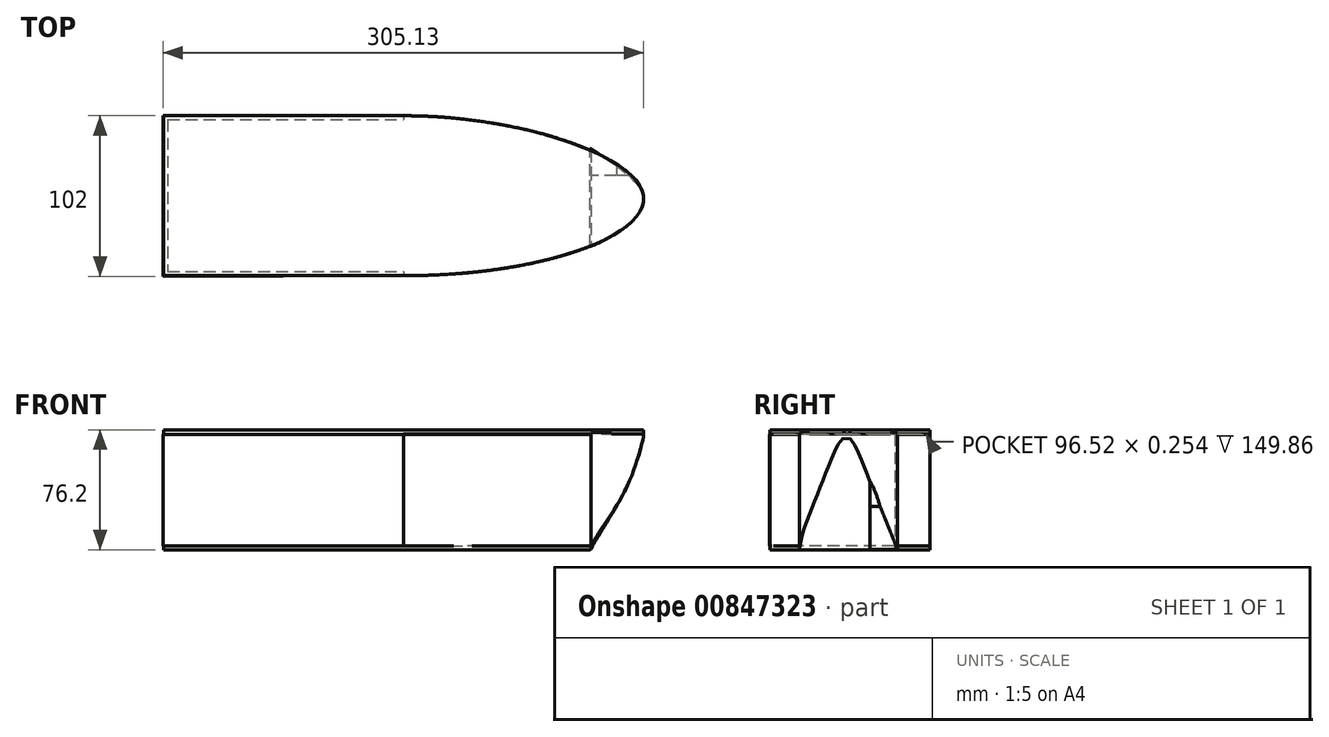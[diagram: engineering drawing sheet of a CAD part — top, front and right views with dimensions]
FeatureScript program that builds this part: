
annotation { "Feature Type Name" : "Feature", "Feature Type Description" : "" }
export const myFeature = defineFeature(function(context is Context, id is Id, definition is map)
    precondition{}
    {
        {
            var Q0;
            Q0=qCreatedBy(makeId("Top.planeOp"),FACE);
            var sketch = newSketch(context, id + "F0", { "sketchPlane" : qUnion([Q0])});
            skLineSegment(sketch, "E0.bottom", {"start": v(-100.95, 38.14) * mm, "end": v(203.85, 38.14) * mm});
            skLineSegment(sketch, "E0.top", {"start": v(-100.95, -63.46) * mm, "end": v(203.85, -63.46) * mm});
            skLineSegment(sketch, "E0.left", {"start": v(-100.95, 38.14) * mm, "end": v(-100.95, -63.46) * mm});
            skLineSegment(sketch, "E0.right", {"start": v(203.85, 38.14) * mm, "end": v(203.85, -63.46) * mm});
            skSolve(sketch);
        }
        {
            var Q0;
            Q0 = qSketchRegion(id + "F0", true);
            extrude(context, id + "F1", {"entities" : qUnion([Q0]), "depth" : 76.2 * mm, "offsetDistance" : 25.4 * mm});
        }
        {
            var Q0;
            Q0=makeQuery(id+"F1.opExtrude","CAP_FACE",FACE,{"disambiguationData":[OSD([sQuery(id+"F0.wireOp",EDGE,"E0.bottom"),sQuery(id+"F0.wireOp",EDGE,"E0.top"),sQuery(id+"F0.wireOp",EDGE,"E0.left"),sQuery(id+"F0.wireOp",EDGE,"E0.right")])],"isStart":false});
            var sketch = newSketch(context, id + "F2", { "sketchPlane" : qUnion([Q0])});
            skFitSpline(sketch, "E1", {"points": [v(51.45, 38.14) * mm, v(203.85, -12.66) * mm, v(51.45, -63.46) * mm], "startDerivative": vector(443.7, 0) * mm, "endDerivative": vector(-531.36, 0) * mm});
            skLineSegment(sketch, "E2", {"start": v(51.45, 38.14) * mm, "end": v(203.85, 38.14) * mm});
            skLineSegment(sketch, "E3", {"start": v(51.45, -63.46) * mm, "end": v(203.85, -63.46) * mm});
            skLineSegment(sketch, "E4", {"start": v(203.85, -63.46) * mm, "end": v(203.85, 38.14) * mm});
            skLineSegment(sketch, "E5", {"start": v(203.85, 38.14) * mm, "end": v(51.45, 38.14) * mm});
            skSolve(sketch);
        }
        {
            var Q0;
            Q0 = qSketchRegion(id + "F2", true);
            extrude(context, id + "F3", {"entities" : qUnion([Q0]), "operationType" : NewBodyOperationType.REMOVE, "endBound" : BoundingType.THROUGH_ALL, "oppositeDirection" : true, "depth" : 25.4 * mm, "offsetDistance" : 25.4 * mm});
        }
        {
            var Q0;
            {var subQ0=sQuery(id+"F2.wireOp",EDGE,"E1");Q0=makeQuery(id+"F3.boolean.opBoolean","COPY",FACE,{"derivedFrom":makeQuery(id+"F3.opExtrude","SWEPT_FACE",FACE,{"disambiguationData":[OSD([subQ0]),TDD([makeQuery(id+"F2.imprint","IMPRINT",EDGE,{"disambiguationData":[TD([[makeQuery(id+"F2.imprint","INTERSECT",VERTEX,{"disambiguationData":[OD(1.0)],"derivedFrom":[subQ0,sQuery(id+"F2.wireOp",EDGE,"E4")]}),-1.0]])],"derivedFrom":subQ0})])]})});}
            var Q1;
            {var subQ0=sQuery(id+"F2.wireOp",EDGE,"E1");Q1=makeQuery(id+"F3.boolean.opBoolean","COPY",FACE,{"derivedFrom":makeQuery(id+"F3.opExtrude","SWEPT_FACE",FACE,{"disambiguationData":[OSD([subQ0]),TDD([makeQuery(id+"F2.imprint","IMPRINT",EDGE,{"disambiguationData":[TD([[makeQuery(id+"F2.imprint","INTERSECT",VERTEX,{"disambiguationData":[OD(0.0)],"derivedFrom":[subQ0,sQuery(id+"F2.wireOp",EDGE,"E4")]}),1.0]])],"derivedFrom":subQ0})])]})});}
            var Q2;
            Q2=makeQuery(id+"F1.opExtrude","SWEPT_FACE",FACE,{"disambiguationData":[OSD([sQuery(id+"F0.wireOp",EDGE,"E0.right")])]});
            shell(context, id + "F4", {"entities" : qUnion([Q0, Q1, Q2]), "thickness" : 2.54 * mm});
        }
        {
            var Q0;
            {var subQ0=sQuery(id+"F0.wireOp",EDGE,"E0.right");var subQ1=sQuery(id+"F0.wireOp",EDGE,"E0.left");var subQ2=sQuery(id+"F0.wireOp",EDGE,"E0.top");var subQ3=sQuery(id+"F0.wireOp",EDGE,"E0.bottom");Q0=makeQuery(id+"F4.opShell","OFFSET_FACE",FACE,{"disambiguationData":[OSD([subQ3,subQ2,subQ1,subQ0]),TDD([makeQuery(id+"F1.opExtrude","CAP_FACE",FACE,{"disambiguationData":[OSD([subQ3,subQ2,subQ1,subQ0])],"isStart":true})])]});}
            var sketch = newSketch(context, id + "F5", { "sketchPlane" : qUnion([Q0])});
            skLineSegment(sketch, "E6.bottom", {"start": v(207.4, -53.9) * mm, "end": v(170.81, -53.9) * mm});
            skLineSegment(sketch, "E6.top", {"start": v(207.4, 69.86) * mm, "end": v(170.81, 69.86) * mm});
            skLineSegment(sketch, "E6.left", {"start": v(207.4, -53.9) * mm, "end": v(207.4, 69.86) * mm});
            skLineSegment(sketch, "E6.right", {"start": v(170.81, -53.9) * mm, "end": v(170.81, 69.86) * mm});
            skSolve(sketch);
        }
        {
            var Q0;
            Q0 = qSketchRegion(id + "F5", true);
            extrude(context, id + "F6", {"entities" : qUnion([Q0]), "operationType" : NewBodyOperationType.REMOVE, "endBound" : BoundingType.THROUGH_ALL, "oppositeDirection" : true, "depth" : 25.4 * mm, "offsetDistance" : 25.4 * mm});
        }
        {
            var Q0;
            {var subQ0=sQuery(id+"F0.wireOp",EDGE,"E0.right");var subQ1=sQuery(id+"F0.wireOp",EDGE,"E0.left");var subQ2=sQuery(id+"F0.wireOp",EDGE,"E0.top");var subQ3=sQuery(id+"F0.wireOp",EDGE,"E0.bottom");Q0=makeQuery(id+"F4.opShell","OFFSET_FACE",FACE,{"disambiguationData":[OSD([subQ3,subQ2,subQ1,subQ0]),TDD([makeQuery(id+"F1.opExtrude","CAP_FACE",FACE,{"disambiguationData":[OSD([subQ3,subQ2,subQ1,subQ0])],"isStart":true})])]});}
            var sketch = newSketch(context, id + "F7", { "sketchPlane" : qUnion([Q0])});
            skLineSegment(sketch, "E7", {"start": v(51.45, -63.46) * mm, "end": v(51.45, -60.92) * mm});
            skLineSegment(sketch, "E8", {"start": v(170.81, 15.8) * mm, "end": v(170.81, -44.36) * mm});
            skFitSpline(sketch, "E9", {"points": [v(51.45, -63.46) * mm, v(83.38, -62.33) * mm, v(115.2, -58.78) * mm, v(138.96, -54.22) * mm, v(157.2, -49.25) * mm, v(164.59, -46.75) * mm, v(170.81, -44.36) * mm], "startDerivative": vector(145.28, 2.52) * mm, "endDerivative": vector(63.35, 23.61) * mm});
            skFitSpline(sketch, "E10", {"points": [v(170.81, 15.8) * mm, v(147.19, 24.44) * mm, v(121.35, 30.96) * mm, v(92.13, 35.7) * mm, v(69.84, 37.63) * mm, v(51.45, 38.14) * mm], "startDerivative": vector(-114.94, 45.24) * mm, "endDerivative": vector(-104.07, 2.3) * mm});
            skLineSegment(sketch, "E11", {"start": v(51.45, 38.14) * mm, "end": v(-101.28, 38.14) * mm});
            skLineSegment(sketch, "E12", {"start": v(-101.28, 38.14) * mm, "end": v(-101.28, -63.86) * mm});
            skLineSegment(sketch, "E13", {"start": v(-101.28, -63.86) * mm, "end": v(51.45, -63.46) * mm});
            skSolve(sketch);
        }
        {
            var Q0;
            Q0 = qSketchRegion(id + "F7", true);
            extrude(context, id + "F8", {"entities" : qUnion([Q0]), "operationType" : NewBodyOperationType.ADD, "depth" : 70.87 * mm, "offsetDistance" : 25.4 * mm});
        }
        {
            var Q0;
            Q0=qCreatedBy(makeId("Top.planeOp"),FACE);
            var sketch = newSketch(context, id + "F9", { "sketchPlane" : qUnion([Q0])});
            skLineSegment(sketch, "E14", {"start": v(170.36, -44.81) * mm, "end": v(170.36, 17.3) * mm});
            skFitSpline(sketch, "E15", {"points": [v(170.36, 17.3) * mm, v(203.8, -15.35) * mm, v(170.36, -44.81) * mm], "startDerivative": vector(99.17, -66.11) * mm, "endDerivative": vector(-96.72, -38.69) * mm});
            skSolve(sketch);
        }
        {
            var Q0;
            Q0 = qSketchRegion(id + "F9", true);
            extrude(context, id + "F10", {"entities" : qUnion([Q0]), "operationType" : NewBodyOperationType.ADD, "depth" : 74.42 * mm, "offsetDistance" : 25.4 * mm});
        }
        {
            var Q0;
            Q0=qCreatedBy(makeId("Front.planeOp"),FACE);
            var sketch = newSketch(context, id + "F11", { "sketchPlane" : qUnion([Q0])});
            skFitSpline(sketch, "E16", {"points": [v(203.29, 77.02) * mm, v(191.34, 38.04) * mm, v(169.96, 0) * mm], "startDerivative": vector(7.68, -149.67) * mm, "endDerivative": vector(-63.06, -42.66) * mm});
            skLineSegment(sketch, "E17", {"start": v(203.29, 77.02) * mm, "end": v(203.29, 0) * mm});
            skLineSegment(sketch, "E18", {"start": v(203.29, 0) * mm, "end": v(169.96, 0) * mm});
            skSolve(sketch);
        }
        {
            var Q0;
            Q0 = qSketchRegion(id + "F11", true);
            extrude(context, id + "F12", {"entities" : qUnion([Q0]), "operationType" : NewBodyOperationType.REMOVE, "endBound" : BoundingType.THROUGH_ALL, "oppositeDirection" : true, "depth" : 25.4 * mm, "offsetDistance" : 25.4 * mm});
        }
        {
            var Q0;
            Q0=makeQuery(id+"F12.boolean.opBoolean","COPY",FACE,{"derivedFrom":makeQuery(id+"F12.opExtrude","CAP_FACE",FACE,{"disambiguationData":[OSD([sQuery(id+"F11.wireOp",EDGE,"E16"),sQuery(id+"F11.wireOp",EDGE,"E17"),sQuery(id+"F11.wireOp",EDGE,"E18")])],"isStart":true})});
            var sketch = newSketch(context, id + "F13", { "sketchPlane" : qUnion([Q0])});
            skFitSpline(sketch, "E19", {"points": [v(-204.86, 76.37) * mm, v(-169.96, 0) * mm], "startDerivative": vector(30.48, -145.24) * mm, "endDerivative": vector(25.46, -63.12) * mm});
            skLineSegment(sketch, "E20", {"start": v(-204.86, 76.37) * mm, "end": v(-204.86, 0) * mm});
            skLineSegment(sketch, "E21", {"start": v(-204.86, 0) * mm, "end": v(-169.96, 0) * mm});
            skSolve(sketch);
        }
        {
            var Q0;
            Q0 = qSketchRegion(id + "F13", true);
            extrude(context, id + "F14", {"entities" : qUnion([Q0]), "operationType" : NewBodyOperationType.REMOVE, "endBound" : BoundingType.THROUGH_ALL, "oppositeDirection" : true, "depth" : 25.4 * mm, "offsetDistance" : 25.4 * mm});
        }
        {
            var Q0;
            Q0=qCreatedBy(makeId("Front.planeOp"),FACE);
            var sketch = newSketch(context, id + "F15", { "sketchPlane" : qUnion([Q0])});
            skFitSpline(sketch, "E22", {"points": [v(204.23, 76.4) * mm, v(170.28, 0) * mm], "startDerivative": vector(-9.43, -96.2) * mm, "endDerivative": vector(-30.18, -57.53) * mm});
            skLineSegment(sketch, "E23", {"start": v(170.28, 0) * mm, "end": v(212.4, 0) * mm});
            skLineSegment(sketch, "E24", {"start": v(212.4, 0) * mm, "end": v(204.23, 76.4) * mm});
            skSolve(sketch);
        }
        {
            var Q0;
            Q0 = qSketchRegion(id + "F15", true);
            extrude(context, id + "F16", {"entities" : qUnion([Q0]), "operationType" : NewBodyOperationType.REMOVE, "endBound" : BoundingType.THROUGH_ALL, "oppositeDirection" : true, "depth" : 25.4 * mm, "offsetDistance" : 25.4 * mm});
        }
    });
